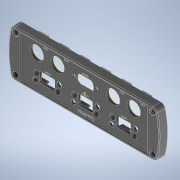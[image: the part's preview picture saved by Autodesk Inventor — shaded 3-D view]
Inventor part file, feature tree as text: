
AUTODESK INVENTOR PART (.ipt)
format: ipt  version: 2021 (Build 250183000, 183)  size: 1,110,016 bytes
history: native  units: mm
features: sketch x10, extrude x9, chamfer x4, fillet x3, plane x2, mirror x1, hole x1, projected_geometry x1, other x1
ambient origin geometry x8: Origin, YZ Plane, XZ Plane, XY Plane, X Axis, Y Axis, Z Axis, Center Point
bodies: Solid1 (feature_tree)
feature tree (32):
  extrude  "Extrusion1"  TaperAngle=0.0deg  [1 undecoded]
  fillet  "Fillet1"  Radius=6.9mm
  plane  "Work Plane1"
  extrude  "Extrusion4"  [1 undecoded]
  chamfer  "Chamfer2"  [1 undecoded]
  mirror  "Mirror1"
  plane  "Work Plane2"
  extrude  "Extrusion6"  Depth=0.2mm
  extrude  "Extrusion7"  Depth=1.0mm
  chamfer  "Chamfer3"  Distance=12.495mm
  extrude  "Extrusion9"  Depth=1.0mm
  fillet  "Fillet3"  Radius=4.77mm
  hole  "Hole1"  [1 undecoded]
  extrude  "Extrusion10"  Depth=1.0mm
  extrude  "Extrusion11"  Depth=1.0mm
  extrude  "Extrusion12"  Depth=1.0mm
  fillet  "Fillet4"  Radius=6.9mm
  chamfer  "Chamfer4"  Distance=10.075mm
  chamfer  "Chamfer5"  Distance=42.584mm
  extrude  "Extrusion13"  Depth=1.0mm
  sketch  "Sketch20"  dims[d54=10.46mm d56=3.3mm d57=12.495mm d58=5.23mm d59=4.77mm d60=0.0mm d61=0.0mm d63=3.72mm d64=9.51mm d65=4.85mm d66=4.85mm d67=27.0mm d68=9.0mm d69=3.3mm d70=3.3mm d71=24.0mm d72=16.55mm d73=11.55mm d74=6.35mm d75=1.85mm d76=5.225mm d77=6.9mm d78=10.075mm d79=10.075mm d80=42.584mm d82=7.0mm d83=10.0mm d84=0.0mm d85=0.5mm d86=2.0mm d87=45.0deg d101=10.075mm d102=4.85mm d103=4.85mm d104=27.0mm d105=9.0mm d106=3.3mm d107=3.3mm d108=24.0mm d109=17.55mm d110=11.55mm d111=6.35mm d112=1.85mm d113=4.725mm d114=10.075mm d115=12.0mm d116=6.9mm d117=42.584mm d118=7.0mm d119=7.0mm d122=12.0mm d123=41.0mm d124=2.0mm d125=0.0mm d126=2.0mm d127=3.25mm d128=6.0mm d129=6.25mm d130=2.0mm d131=90.0deg d132=8.0mm d133=20.594885mm d134=10.0mm d135=0.0mm d136=10.0mm d137=0.0mm d138=0.2mm d139=0.0mm d140=3.0mm d141=0.2mm d142=2.0mm d143=45.0deg d144=0.2mm d145=2.0mm d146=45.0deg d147=10.0mm d148=0.0mm d149=8.0mm d150=12.5mm d151=8.0mm d152=12.5mm d153=12.5mm d154=8.0mm d155=8.0mm d156=12.5mm d157=4.5mm d160=4.5mm d161=1.0mm d164=1.0mm d165=1.0mm d166=2.25mm d167=28.699852mm d169=20.0mm d171=42.584mm d172=10.0mm d174=10.0mm d176=7.0mm d177=7.0mm d178=7.0mm d179=1.0mm d180=4.5mm d181=4.725mm]
  sketch  "Sketch1"  dims[d3=9.0mm d15=0.0mm d16=0.0mm d21=6.9mm]
  sketch  "Sketch5"  dims[d23=1.35mm d26=-1.5mm]
  sketch  "Sketch8"  dims[d40=15.4mm]
  sketch  "Sketch14"  dims[d41=11.5mm]
  sketch  "Sketch15"  dims[d42=54.0mm]
  sketch  "Sketch16"  dims[d43=15.4mm]
  projected_geometry  "Projected Loop5"
  sketch  "Sketch17"  dims[d44=0.0mm]
  sketch  "Sketch18"  dims[d45=31.0mm d46=0.0mm d47=0.0mm]
  sketch  "Sketch19"  dims[d48=0.2mm d49=2.0mm d50=45.0deg d53=1.745329mm]
  other  "1009799_3D"
note: 4 required parameter values undecoded (feature->parameter linkage not recoverable at this tier; creation-order binding heuristic only, values carry confidence <= 0.55)
